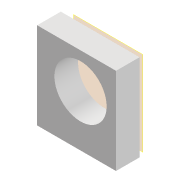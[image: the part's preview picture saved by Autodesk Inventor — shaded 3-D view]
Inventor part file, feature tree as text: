
AUTODESK INVENTOR PART (.ipt)
format: ipt  version: 2022 (Build 260153000, 153)  size: 95,232 bytes
history: native  units: mm
features: other x3, reference x2, plane x1, extrude x1, sketch x1
ambient origin geometry x8: Origin, YZ Plane, XZ Plane, XY Plane, X Axis, Y Axis, Z Axis, Center Point
bodies: Volumenkörper1 (feature_tree)
feature tree (8):
  plane  "Arbeitsebene1"
  extrude  "Extrusion1"  Depth=20.0mm
  sketch  "Skizze1"  dims[d0=20.0mm d1=20.0mm d2=13.25mm d4=1.0mm d5=6.0mm d6=0.0mm d7=20.0mm d8=2.0mm d9=1.0mm]
  reference  "Referenz1"
  reference  "Referenz2"
  other  "Assemlby_lightsheet_generator_passive_v2.iam"
  other  "30_Lightsheet_generator_passive_base_v1:1"
  other  "00_SMAConnector_fiber copy:1"
